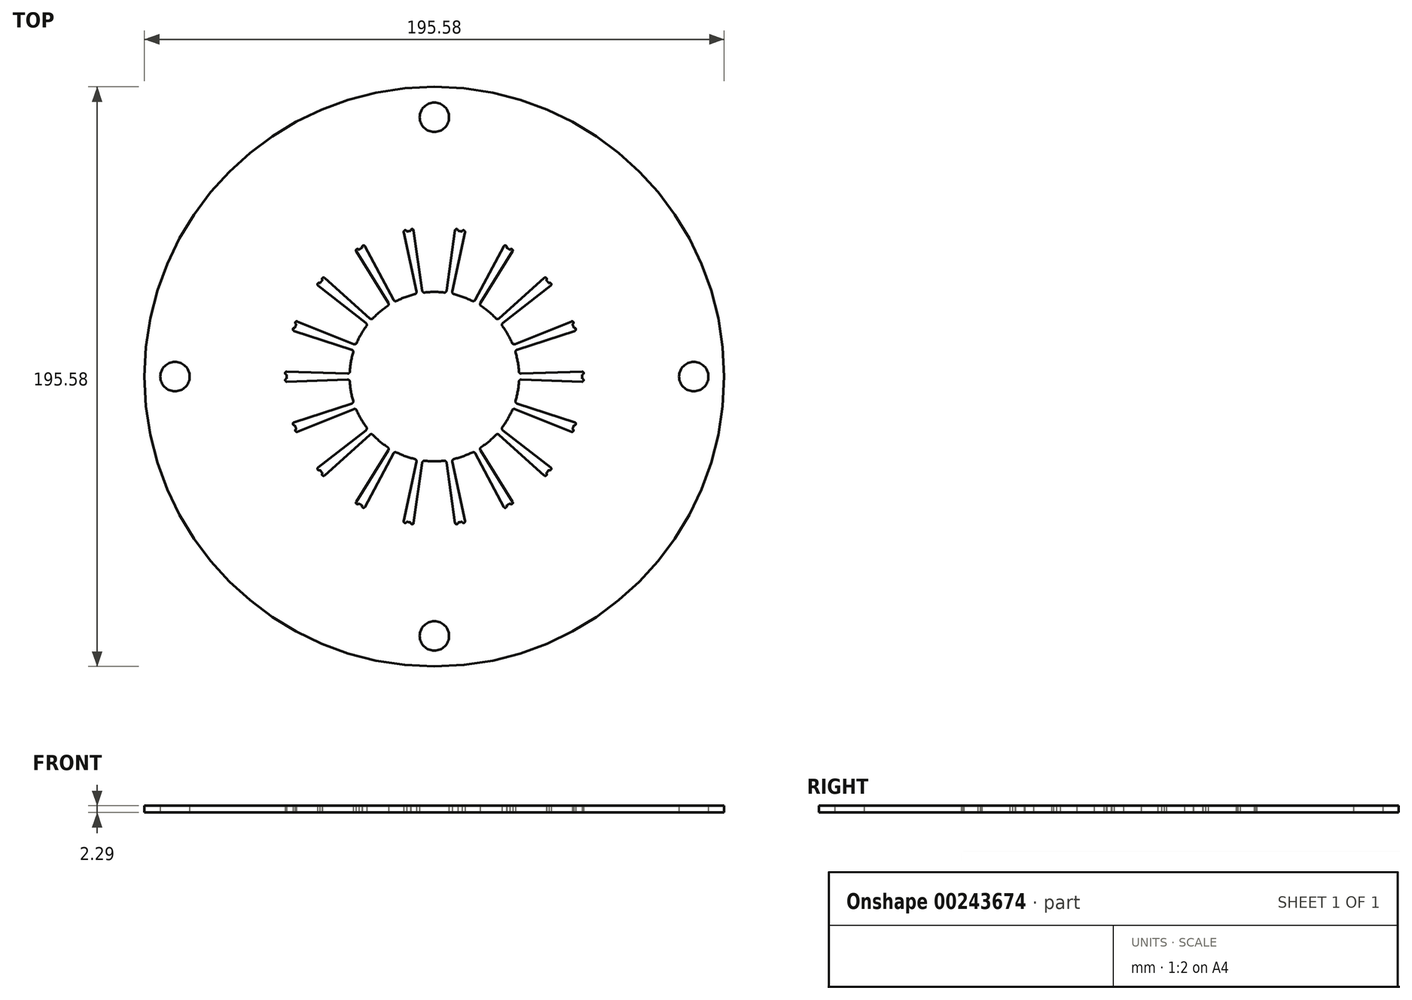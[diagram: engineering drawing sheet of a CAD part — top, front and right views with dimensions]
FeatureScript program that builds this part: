
annotation { "Feature Type Name" : "Feature", "Feature Type Description" : "" }
export const myFeature = defineFeature(function(context is Context, id is Id, definition is map)
    precondition{}
    {
        {
            var Q0;
            Q0=qCreatedBy(makeId("Top.planeOp"),FACE);
            var sketch = newSketch(context, id + "F0", { "sketchPlane" : qUnion([Q0])});
            skCircle(sketch, "E0", {"center": v(0, 0) * mm, "radius": 97.8 * mm});
            skLineSegment(sketch, "E1", {"start": v(0, 0) * mm, "end": v(0, 87.5) * mm, "construction": true});
            skCircle(sketch, "E2", {"center": v(0, 87.5) * mm, "radius": 4.95 * mm});
            skCircle(sketch, "E3.1.0", {"center": v(-87.5, 0) * mm, "radius": 4.95 * mm});
            skCircle(sketch, "E3.2.0", {"center": v(0, -87.5) * mm, "radius": 4.95 * mm});
            skCircle(sketch, "E3.3.0", {"center": v(87.5, 0) * mm, "radius": 4.95 * mm});
            skCircle(sketch, "E4", {"center": v(0, 0) * mm, "radius": 49.85 * mm});
            skCircle(sketch, "E5", {"center": v(0, 0) * mm, "radius": 12.7 * mm});
            skLineSegment(sketch, "E6", {"start": v(-6.99, 49.36) * mm, "end": v(-1.78, 12.57) * mm});
            skLineSegment(sketch, "E7", {"start": v(1.78, 12.57) * mm, "end": v(6.98, 49.36) * mm});
            skLineSegment(sketch, "E8", {"start": v(6.98, 49.36) * mm, "end": v(0, 50.34) * mm, "construction": true});
            skLineSegment(sketch, "E9", {"start": v(0, 50.34) * mm, "end": v(-6.99, 49.36) * mm, "construction": true});
            skLineSegment(sketch, "E10", {"start": v(-6.99, 49.36) * mm, "end": v(6.99, 49.36) * mm, "construction": true});
            skCircle(sketch, "E11", {"center": v(0, 0) * mm, "radius": 28.58 * mm});
            skLineSegment(sketch, "E12.1.0", {"start": v(-23.44, 44) * mm, "end": v(-5.97, 11.2) * mm});
            skLineSegment(sketch, "E12.1.1", {"start": v(-2.63, 12.43) * mm, "end": v(-10.32, 48.77) * mm});
            skLineSegment(sketch, "E12.2.0", {"start": v(-37.08, 33.32) * mm, "end": v(-9.45, 8.49) * mm});
            skLineSegment(sketch, "E12.2.1", {"start": v(-6.72, 10.78) * mm, "end": v(-26.37, 42.3) * mm});
            skLineSegment(sketch, "E12.3.0", {"start": v(-46.24, 18.63) * mm, "end": v(-11.78, 4.75) * mm});
            skLineSegment(sketch, "E12.3.1", {"start": v(-10, 7.83) * mm, "end": v(-39.25, 30.73) * mm});
            skLineSegment(sketch, "E12.4.0", {"start": v(-49.82, 1.7) * mm, "end": v(-12.7, 0.43) * mm});
            skLineSegment(sketch, "E12.4.1", {"start": v(-12.07, 3.94) * mm, "end": v(-47.4, 15.45) * mm});
            skLineSegment(sketch, "E12.5.0", {"start": v(-47.4, -15.45) * mm, "end": v(-12.07, -3.94) * mm});
            skLineSegment(sketch, "E12.5.1", {"start": v(-12.7, -0.43) * mm, "end": v(-49.82, -1.7) * mm});
            skLineSegment(sketch, "E12.6.0", {"start": v(-39.25, -30.73) * mm, "end": v(-10, -7.83) * mm});
            skLineSegment(sketch, "E12.6.1", {"start": v(-11.78, -4.75) * mm, "end": v(-46.24, -18.63) * mm});
            skLineSegment(sketch, "E12.7.0", {"start": v(-26.37, -42.3) * mm, "end": v(-6.72, -10.78) * mm});
            skLineSegment(sketch, "E12.7.1", {"start": v(-9.45, -8.49) * mm, "end": v(-37.08, -33.32) * mm});
            skLineSegment(sketch, "E12.8.0", {"start": v(-10.32, -48.77) * mm, "end": v(-2.63, -12.43) * mm});
            skLineSegment(sketch, "E12.8.1", {"start": v(-5.97, -11.2) * mm, "end": v(-23.44, -44) * mm});
            skLineSegment(sketch, "E12.9.0", {"start": v(6.98, -49.36) * mm, "end": v(1.78, -12.57) * mm});
            skLineSegment(sketch, "E12.9.1", {"start": v(-1.78, -12.57) * mm, "end": v(-6.99, -49.36) * mm});
            skLineSegment(sketch, "E12.10.0", {"start": v(23.44, -44) * mm, "end": v(5.97, -11.2) * mm});
            skLineSegment(sketch, "E12.10.1", {"start": v(2.63, -12.43) * mm, "end": v(10.32, -48.77) * mm});
            skLineSegment(sketch, "E12.11.0", {"start": v(37.08, -33.32) * mm, "end": v(9.45, -8.49) * mm});
            skLineSegment(sketch, "E12.11.1", {"start": v(6.72, -10.78) * mm, "end": v(26.37, -42.3) * mm});
            skLineSegment(sketch, "E12.12.0", {"start": v(46.24, -18.63) * mm, "end": v(11.78, -4.75) * mm});
            skLineSegment(sketch, "E12.12.1", {"start": v(10, -7.83) * mm, "end": v(39.25, -30.73) * mm});
            skLineSegment(sketch, "E12.13.0", {"start": v(49.82, -1.7) * mm, "end": v(12.7, -0.43) * mm});
            skLineSegment(sketch, "E12.13.1", {"start": v(12.07, -3.94) * mm, "end": v(47.4, -15.45) * mm});
            skLineSegment(sketch, "E12.14.0", {"start": v(47.4, 15.45) * mm, "end": v(12.07, 3.94) * mm});
            skLineSegment(sketch, "E12.14.1", {"start": v(12.7, 0.43) * mm, "end": v(49.82, 1.7) * mm});
            skLineSegment(sketch, "E12.15.0", {"start": v(39.25, 30.73) * mm, "end": v(10, 7.83) * mm});
            skLineSegment(sketch, "E12.15.1", {"start": v(11.78, 4.75) * mm, "end": v(46.24, 18.63) * mm});
            skLineSegment(sketch, "E12.16.0", {"start": v(26.37, 42.3) * mm, "end": v(6.72, 10.78) * mm});
            skLineSegment(sketch, "E12.16.1", {"start": v(9.45, 8.49) * mm, "end": v(37.08, 33.32) * mm});
            skLineSegment(sketch, "E12.17.0", {"start": v(10.32, 48.77) * mm, "end": v(2.63, 12.43) * mm});
            skLineSegment(sketch, "E12.17.1", {"start": v(5.97, 11.2) * mm, "end": v(23.44, 44) * mm});
            skSolve(sketch);
        }
        {
            var Q0;
            Q0=makeQuery(id+"F0.imprint","IMPRINT",FACE,{"disambiguationData":[TD([[makeQuery(id+"F0.imprint","IMPRINT",EDGE,{"derivedFrom":sQuery(id+"F0.wireOp",EDGE,"E0")}),1.0]])]});
            var Q1;
            {var subQ0=sQuery(id+"F0.wireOp",EDGE,"E12.15.0");var subQ1=sQuery(id+"F0.wireOp",EDGE,"E4");var subQ2=makeQuery(id+"F0.imprint","INTERSECT",VERTEX,{"derivedFrom":[subQ1,subQ0]});Q1=makeQuery(id+"F0.imprint","IMPRINT",FACE,{"disambiguationData":[TD([[makeQuery(id+"F0.imprint","IMPRINT",EDGE,{"disambiguationData":[TD([[subQ2,1.0]])],"derivedFrom":subQ1}),1.0]])]});}
            var Q2;
            {var subQ0=sQuery(id+"F0.wireOp",EDGE,"E12.16.0");var subQ1=sQuery(id+"F0.wireOp",EDGE,"E4");var subQ2=makeQuery(id+"F0.imprint","INTERSECT",VERTEX,{"derivedFrom":[subQ1,subQ0]});Q2=makeQuery(id+"F0.imprint","IMPRINT",FACE,{"disambiguationData":[TD([[makeQuery(id+"F0.imprint","IMPRINT",EDGE,{"disambiguationData":[TD([[subQ2,1.0]])],"derivedFrom":subQ1}),1.0]])]});}
            var Q3;
            {var subQ0=sQuery(id+"F0.wireOp",EDGE,"E12.17.0");var subQ1=sQuery(id+"F0.wireOp",EDGE,"E4");var subQ2=makeQuery(id+"F0.imprint","INTERSECT",VERTEX,{"derivedFrom":[subQ1,subQ0]});Q3=makeQuery(id+"F0.imprint","IMPRINT",FACE,{"disambiguationData":[TD([[makeQuery(id+"F0.imprint","IMPRINT",EDGE,{"disambiguationData":[TD([[subQ2,1.0]])],"derivedFrom":subQ1}),1.0]])]});}
            var Q4;
            {var subQ0=sQuery(id+"F0.wireOp",EDGE,"E6");var subQ1=sQuery(id+"F0.wireOp",EDGE,"E4");var subQ2=makeQuery(id+"F0.imprint","INTERSECT",VERTEX,{"derivedFrom":[subQ1,subQ0]});Q4=makeQuery(id+"F0.imprint","IMPRINT",FACE,{"disambiguationData":[TD([[makeQuery(id+"F0.imprint","IMPRINT",EDGE,{"disambiguationData":[TD([[subQ2,1.0]])],"derivedFrom":subQ1}),1.0]])]});}
            var Q5;
            {var subQ0=sQuery(id+"F0.wireOp",EDGE,"E12.1.0");var subQ1=sQuery(id+"F0.wireOp",EDGE,"E4");var subQ2=makeQuery(id+"F0.imprint","INTERSECT",VERTEX,{"derivedFrom":[subQ1,subQ0]});Q5=makeQuery(id+"F0.imprint","IMPRINT",FACE,{"disambiguationData":[TD([[makeQuery(id+"F0.imprint","IMPRINT",EDGE,{"disambiguationData":[TD([[subQ2,1.0]])],"derivedFrom":subQ1}),1.0]])]});}
            var Q6;
            {var subQ0=sQuery(id+"F0.wireOp",EDGE,"E12.2.0");var subQ1=sQuery(id+"F0.wireOp",EDGE,"E4");var subQ2=makeQuery(id+"F0.imprint","INTERSECT",VERTEX,{"derivedFrom":[subQ1,subQ0]});Q6=makeQuery(id+"F0.imprint","IMPRINT",FACE,{"disambiguationData":[TD([[makeQuery(id+"F0.imprint","IMPRINT",EDGE,{"disambiguationData":[TD([[subQ2,1.0]])],"derivedFrom":subQ1}),1.0]])]});}
            var Q7;
            {var subQ0=sQuery(id+"F0.wireOp",EDGE,"E12.3.0");var subQ1=sQuery(id+"F0.wireOp",EDGE,"E4");var subQ2=makeQuery(id+"F0.imprint","INTERSECT",VERTEX,{"derivedFrom":[subQ1,subQ0]});Q7=makeQuery(id+"F0.imprint","IMPRINT",FACE,{"disambiguationData":[TD([[makeQuery(id+"F0.imprint","IMPRINT",EDGE,{"disambiguationData":[TD([[subQ2,1.0]])],"derivedFrom":subQ1}),1.0]])]});}
            var Q8;
            {var subQ0=sQuery(id+"F0.wireOp",EDGE,"E12.4.0");var subQ1=sQuery(id+"F0.wireOp",EDGE,"E4");var subQ2=makeQuery(id+"F0.imprint","INTERSECT",VERTEX,{"derivedFrom":[subQ1,subQ0]});Q8=makeQuery(id+"F0.imprint","IMPRINT",FACE,{"disambiguationData":[TD([[makeQuery(id+"F0.imprint","IMPRINT",EDGE,{"disambiguationData":[TD([[subQ2,1.0]])],"derivedFrom":subQ1}),1.0]])]});}
            var Q9;
            {var subQ0=sQuery(id+"F0.wireOp",EDGE,"E12.5.0");var subQ1=sQuery(id+"F0.wireOp",EDGE,"E4");var subQ2=makeQuery(id+"F0.imprint","INTERSECT",VERTEX,{"derivedFrom":[subQ1,subQ0]});Q9=makeQuery(id+"F0.imprint","IMPRINT",FACE,{"disambiguationData":[TD([[makeQuery(id+"F0.imprint","IMPRINT",EDGE,{"disambiguationData":[TD([[subQ2,1.0]])],"derivedFrom":subQ1}),1.0]])]});}
            var Q10;
            {var subQ0=sQuery(id+"F0.wireOp",EDGE,"E12.6.0");var subQ1=sQuery(id+"F0.wireOp",EDGE,"E4");var subQ2=makeQuery(id+"F0.imprint","INTERSECT",VERTEX,{"derivedFrom":[subQ1,subQ0]});Q10=makeQuery(id+"F0.imprint","IMPRINT",FACE,{"disambiguationData":[TD([[makeQuery(id+"F0.imprint","IMPRINT",EDGE,{"disambiguationData":[TD([[subQ2,1.0]])],"derivedFrom":subQ1}),1.0]])]});}
            var Q11;
            {var subQ0=sQuery(id+"F0.wireOp",EDGE,"E12.7.0");var subQ1=sQuery(id+"F0.wireOp",EDGE,"E4");var subQ2=makeQuery(id+"F0.imprint","INTERSECT",VERTEX,{"derivedFrom":[subQ1,subQ0]});Q11=makeQuery(id+"F0.imprint","IMPRINT",FACE,{"disambiguationData":[TD([[makeQuery(id+"F0.imprint","IMPRINT",EDGE,{"disambiguationData":[TD([[subQ2,1.0]])],"derivedFrom":subQ1}),1.0]])]});}
            var Q12;
            {var subQ0=sQuery(id+"F0.wireOp",EDGE,"E12.8.0");var subQ1=sQuery(id+"F0.wireOp",EDGE,"E4");var subQ2=makeQuery(id+"F0.imprint","INTERSECT",VERTEX,{"derivedFrom":[subQ1,subQ0]});Q12=makeQuery(id+"F0.imprint","IMPRINT",FACE,{"disambiguationData":[TD([[makeQuery(id+"F0.imprint","IMPRINT",EDGE,{"disambiguationData":[TD([[subQ2,1.0]])],"derivedFrom":subQ1}),1.0]])]});}
            var Q13;
            {var subQ0=sQuery(id+"F0.wireOp",EDGE,"E12.9.0");var subQ1=sQuery(id+"F0.wireOp",EDGE,"E4");var subQ2=makeQuery(id+"F0.imprint","INTERSECT",VERTEX,{"derivedFrom":[subQ1,subQ0]});Q13=makeQuery(id+"F0.imprint","IMPRINT",FACE,{"disambiguationData":[TD([[makeQuery(id+"F0.imprint","IMPRINT",EDGE,{"disambiguationData":[TD([[subQ2,1.0]])],"derivedFrom":subQ1}),1.0]])]});}
            var Q14;
            {var subQ0=sQuery(id+"F0.wireOp",EDGE,"E12.10.0");var subQ1=sQuery(id+"F0.wireOp",EDGE,"E4");var subQ2=makeQuery(id+"F0.imprint","INTERSECT",VERTEX,{"derivedFrom":[subQ1,subQ0]});Q14=makeQuery(id+"F0.imprint","IMPRINT",FACE,{"disambiguationData":[TD([[makeQuery(id+"F0.imprint","IMPRINT",EDGE,{"disambiguationData":[TD([[subQ2,1.0]])],"derivedFrom":subQ1}),1.0]])]});}
            var Q15;
            {var subQ0=sQuery(id+"F0.wireOp",EDGE,"E12.11.0");var subQ1=sQuery(id+"F0.wireOp",EDGE,"E4");var subQ2=makeQuery(id+"F0.imprint","INTERSECT",VERTEX,{"derivedFrom":[subQ1,subQ0]});Q15=makeQuery(id+"F0.imprint","IMPRINT",FACE,{"disambiguationData":[TD([[makeQuery(id+"F0.imprint","IMPRINT",EDGE,{"disambiguationData":[TD([[subQ2,1.0]])],"derivedFrom":subQ1}),1.0]])]});}
            var Q16;
            {var subQ0=sQuery(id+"F0.wireOp",EDGE,"E12.12.0");var subQ1=sQuery(id+"F0.wireOp",EDGE,"E4");var subQ2=makeQuery(id+"F0.imprint","INTERSECT",VERTEX,{"derivedFrom":[subQ1,subQ0]});Q16=makeQuery(id+"F0.imprint","IMPRINT",FACE,{"disambiguationData":[TD([[makeQuery(id+"F0.imprint","IMPRINT",EDGE,{"disambiguationData":[TD([[subQ2,1.0]])],"derivedFrom":subQ1}),1.0]])]});}
            var Q17;
            {var subQ0=sQuery(id+"F0.wireOp",EDGE,"E12.13.0");var subQ1=sQuery(id+"F0.wireOp",EDGE,"E4");var subQ2=makeQuery(id+"F0.imprint","INTERSECT",VERTEX,{"derivedFrom":[subQ1,subQ0]});Q17=makeQuery(id+"F0.imprint","IMPRINT",FACE,{"disambiguationData":[TD([[makeQuery(id+"F0.imprint","IMPRINT",EDGE,{"disambiguationData":[TD([[subQ2,1.0]])],"derivedFrom":subQ1}),1.0]])]});}
            var Q18;
            {var subQ0=sQuery(id+"F0.wireOp",EDGE,"E12.14.0");var subQ1=sQuery(id+"F0.wireOp",EDGE,"E4");var subQ2=makeQuery(id+"F0.imprint","INTERSECT",VERTEX,{"derivedFrom":[subQ1,subQ0]});Q18=makeQuery(id+"F0.imprint","IMPRINT",FACE,{"disambiguationData":[TD([[makeQuery(id+"F0.imprint","IMPRINT",EDGE,{"disambiguationData":[TD([[subQ2,1.0]])],"derivedFrom":subQ1}),1.0]])]});}
            extrude(context, id + "F1", {"entities" : qUnion([Q0, Q1, Q2, Q3, Q4, Q5, Q6, Q7, Q8, Q9, Q10, Q11, Q12, Q13, Q14, Q15, Q16, Q17, Q18]), "depth" : 2.3 * mm});
        }
        {
            var Q0;
            Q0=makeQuery(id+"F1.opExtrude","CAP_FACE",FACE,{"disambiguationData":[OSD([sQuery(id+"F0.wireOp",EDGE,"E0"),sQuery(id+"F0.wireOp",EDGE,"E2"),sQuery(id+"F0.wireOp",EDGE,"E3.1.0"),sQuery(id+"F0.wireOp",EDGE,"E3.2.0"),sQuery(id+"F0.wireOp",EDGE,"E3.3.0"),sQuery(id+"F0.wireOp",EDGE,"E4"),sQuery(id+"F0.wireOp",EDGE,"E6"),sQuery(id+"F0.wireOp",EDGE,"E7"),sQuery(id+"F0.wireOp",EDGE,"E11"),sQuery(id+"F0.wireOp",EDGE,"E12.1.0"),sQuery(id+"F0.wireOp",EDGE,"E12.1.1"),sQuery(id+"F0.wireOp",EDGE,"E12.2.0"),sQuery(id+"F0.wireOp",EDGE,"E12.2.1"),sQuery(id+"F0.wireOp",EDGE,"E12.3.0"),sQuery(id+"F0.wireOp",EDGE,"E12.3.1"),sQuery(id+"F0.wireOp",EDGE,"E12.4.0"),sQuery(id+"F0.wireOp",EDGE,"E12.4.1"),sQuery(id+"F0.wireOp",EDGE,"E12.5.0"),sQuery(id+"F0.wireOp",EDGE,"E12.5.1"),sQuery(id+"F0.wireOp",EDGE,"E12.6.0"),sQuery(id+"F0.wireOp",EDGE,"E12.6.1"),sQuery(id+"F0.wireOp",EDGE,"E12.7.0"),sQuery(id+"F0.wireOp",EDGE,"E12.7.1"),sQuery(id+"F0.wireOp",EDGE,"E12.8.0"),sQuery(id+"F0.wireOp",EDGE,"E12.8.1"),sQuery(id+"F0.wireOp",EDGE,"E12.9.0"),sQuery(id+"F0.wireOp",EDGE,"E12.9.1"),sQuery(id+"F0.wireOp",EDGE,"E12.10.0"),sQuery(id+"F0.wireOp",EDGE,"E12.10.1"),sQuery(id+"F0.wireOp",EDGE,"E12.11.0"),sQuery(id+"F0.wireOp",EDGE,"E12.11.1"),sQuery(id+"F0.wireOp",EDGE,"E12.12.0"),sQuery(id+"F0.wireOp",EDGE,"E12.12.1"),sQuery(id+"F0.wireOp",EDGE,"E12.13.0"),sQuery(id+"F0.wireOp",EDGE,"E12.13.1"),sQuery(id+"F0.wireOp",EDGE,"E12.14.0"),sQuery(id+"F0.wireOp",EDGE,"E12.14.1"),sQuery(id+"F0.wireOp",EDGE,"E12.15.0"),sQuery(id+"F0.wireOp",EDGE,"E12.15.1"),sQuery(id+"F0.wireOp",EDGE,"E12.16.0"),sQuery(id+"F0.wireOp",EDGE,"E12.16.1"),sQuery(id+"F0.wireOp",EDGE,"E12.17.0"),sQuery(id+"F0.wireOp",EDGE,"E12.17.1")])],"isStart":true});
            var sketch = newSketch(context, id + "F2", { "sketchPlane" : qUnion([Q0])});
            skArc(sketch, "E13", {"start": v(-7.99, -49.2) * mm, "mid": v(-7.56, -49.79) * mm, "end": v(-6.98, -49.36) * mm});
            skArc(sketch, "E14", {"start": v(-10.32, -48.77) * mm, "mid": v(-9.92, -49.37) * mm, "end": v(-9.32, -48.97) * mm});
            skCircle(sketch, "E15", {"center": v(0, 0) * mm, "radius": 49.85 * mm});
            skArc(sketch, "E16.1.0", {"start": v(6.99, -49.36) * mm, "mid": v(7.56, -49.79) * mm, "end": v(7.99, -49.2) * mm});
            skArc(sketch, "E16.1.1", {"start": v(9.32, -48.97) * mm, "mid": v(9.92, -49.37) * mm, "end": v(10.32, -48.77) * mm});
            skArc(sketch, "E16.2.0", {"start": v(23.44, -44) * mm, "mid": v(24.14, -44.2) * mm, "end": v(24.34, -43.5) * mm});
            skArc(sketch, "E16.2.1", {"start": v(25.5, -42.83) * mm, "mid": v(26.2, -43) * mm, "end": v(26.37, -42.3) * mm});
            skArc(sketch, "E16.3.0", {"start": v(37.08, -33.32) * mm, "mid": v(37.8, -33.28) * mm, "end": v(37.75, -32.56) * mm});
            skArc(sketch, "E16.3.1", {"start": v(38.62, -31.52) * mm, "mid": v(39.33, -31.44) * mm, "end": v(39.25, -30.73) * mm});
            skArc(sketch, "E16.4.0", {"start": v(46.24, -18.63) * mm, "mid": v(46.9, -18.34) * mm, "end": v(46.6, -17.68) * mm});
            skArc(sketch, "E16.4.1", {"start": v(47.07, -16.41) * mm, "mid": v(47.72, -16.1) * mm, "end": v(47.4, -15.45) * mm});
            skArc(sketch, "E16.5.0", {"start": v(49.82, -1.7) * mm, "mid": v(50.34, -1.2) * mm, "end": v(49.84, -0.68) * mm});
            skArc(sketch, "E16.5.1", {"start": v(49.84, 0.68) * mm, "mid": v(50.34, 1.2) * mm, "end": v(49.82, 1.7) * mm});
            skArc(sketch, "E16.6.0", {"start": v(47.4, 15.45) * mm, "mid": v(47.72, 16.1) * mm, "end": v(47.07, 16.41) * mm});
            skArc(sketch, "E16.6.1", {"start": v(46.6, 17.68) * mm, "mid": v(46.9, 18.34) * mm, "end": v(46.24, 18.63) * mm});
            skArc(sketch, "E16.7.0", {"start": v(39.25, 30.73) * mm, "mid": v(39.33, 31.44) * mm, "end": v(38.62, 31.52) * mm});
            skArc(sketch, "E16.7.1", {"start": v(37.75, 32.56) * mm, "mid": v(37.8, 33.28) * mm, "end": v(37.08, 33.32) * mm});
            skArc(sketch, "E16.8.0", {"start": v(26.37, 42.3) * mm, "mid": v(26.2, 43) * mm, "end": v(25.5, 42.83) * mm});
            skArc(sketch, "E16.8.1", {"start": v(24.34, 43.5) * mm, "mid": v(24.14, 44.2) * mm, "end": v(23.44, 44) * mm});
            skArc(sketch, "E16.9.0", {"start": v(10.32, 48.77) * mm, "mid": v(9.92, 49.37) * mm, "end": v(9.32, 48.97) * mm});
            skArc(sketch, "E16.9.1", {"start": v(7.99, 49.2) * mm, "mid": v(7.56, 49.79) * mm, "end": v(6.99, 49.36) * mm});
            skArc(sketch, "E16.10.0", {"start": v(-6.99, 49.36) * mm, "mid": v(-7.56, 49.79) * mm, "end": v(-7.99, 49.2) * mm});
            skArc(sketch, "E16.10.1", {"start": v(-9.32, 48.97) * mm, "mid": v(-9.92, 49.37) * mm, "end": v(-10.32, 48.77) * mm});
            skArc(sketch, "E16.11.0", {"start": v(-23.44, 44) * mm, "mid": v(-24.14, 44.2) * mm, "end": v(-24.34, 43.5) * mm});
            skArc(sketch, "E16.11.1", {"start": v(-25.5, 42.83) * mm, "mid": v(-26.2, 43) * mm, "end": v(-26.37, 42.3) * mm});
            skArc(sketch, "E16.12.0", {"start": v(-37.08, 33.32) * mm, "mid": v(-37.8, 33.28) * mm, "end": v(-37.75, 32.56) * mm});
            skArc(sketch, "E16.12.1", {"start": v(-38.62, 31.52) * mm, "mid": v(-39.33, 31.44) * mm, "end": v(-39.25, 30.73) * mm});
            skArc(sketch, "E16.13.0", {"start": v(-46.24, 18.63) * mm, "mid": v(-46.9, 18.34) * mm, "end": v(-46.6, 17.68) * mm});
            skArc(sketch, "E16.13.1", {"start": v(-47.07, 16.41) * mm, "mid": v(-47.72, 16.1) * mm, "end": v(-47.4, 15.45) * mm});
            skArc(sketch, "E16.14.0", {"start": v(-49.82, 1.7) * mm, "mid": v(-50.34, 1.2) * mm, "end": v(-49.84, 0.68) * mm});
            skArc(sketch, "E16.14.1", {"start": v(-49.84, -0.68) * mm, "mid": v(-50.34, -1.2) * mm, "end": v(-49.82, -1.7) * mm});
            skArc(sketch, "E16.15.0", {"start": v(-47.4, -15.45) * mm, "mid": v(-47.72, -16.1) * mm, "end": v(-47.07, -16.41) * mm});
            skArc(sketch, "E16.15.1", {"start": v(-46.6, -17.68) * mm, "mid": v(-46.9, -18.34) * mm, "end": v(-46.24, -18.63) * mm});
            skArc(sketch, "E16.16.0", {"start": v(-39.25, -30.73) * mm, "mid": v(-39.33, -31.44) * mm, "end": v(-38.62, -31.52) * mm});
            skArc(sketch, "E16.16.1", {"start": v(-37.75, -32.56) * mm, "mid": v(-37.8, -33.28) * mm, "end": v(-37.08, -33.32) * mm});
            skArc(sketch, "E16.17.0", {"start": v(-26.37, -42.3) * mm, "mid": v(-26.2, -43) * mm, "end": v(-25.5, -42.83) * mm});
            skArc(sketch, "E16.17.1", {"start": v(-24.34, -43.5) * mm, "mid": v(-24.14, -44.2) * mm, "end": v(-23.44, -44) * mm});
            skSolve(sketch);
        }
        {
            var Q0;
            {var subQ0=sQuery(id+"F2.wireOp",EDGE,"E16.4.0");Q0=makeQuery(id+"F2.imprint","IMPRINT",FACE,{"disambiguationData":[TD([[makeQuery(id+"F2.imprint","IMPRINT",EDGE,{"derivedFrom":subQ0}),1.0]])]});}
            var Q1;
            {var subQ0=sQuery(id+"F2.wireOp",EDGE,"E16.3.1");Q1=makeQuery(id+"F2.imprint","IMPRINT",FACE,{"disambiguationData":[TD([[makeQuery(id+"F2.imprint","IMPRINT",EDGE,{"derivedFrom":subQ0}),1.0]])]});}
            var Q2;
            {var subQ0=sQuery(id+"F2.wireOp",EDGE,"E16.3.0");Q2=makeQuery(id+"F2.imprint","IMPRINT",FACE,{"disambiguationData":[TD([[makeQuery(id+"F2.imprint","IMPRINT",EDGE,{"derivedFrom":subQ0}),1.0]])]});}
            var Q3;
            {var subQ0=sQuery(id+"F2.wireOp",EDGE,"E16.2.1");Q3=makeQuery(id+"F2.imprint","IMPRINT",FACE,{"disambiguationData":[TD([[makeQuery(id+"F2.imprint","IMPRINT",EDGE,{"derivedFrom":subQ0}),1.0]])]});}
            var Q4;
            {var subQ0=sQuery(id+"F2.wireOp",EDGE,"E16.2.0");Q4=makeQuery(id+"F2.imprint","IMPRINT",FACE,{"disambiguationData":[TD([[makeQuery(id+"F2.imprint","IMPRINT",EDGE,{"derivedFrom":subQ0}),1.0]])]});}
            var Q5;
            {var subQ0=sQuery(id+"F2.wireOp",EDGE,"E16.1.0");Q5=makeQuery(id+"F2.imprint","IMPRINT",FACE,{"disambiguationData":[TD([[makeQuery(id+"F2.imprint","IMPRINT",EDGE,{"derivedFrom":subQ0}),1.0]])]});}
            var Q6;
            {var subQ0=sQuery(id+"F2.wireOp",EDGE,"E16.1.1");Q6=makeQuery(id+"F2.imprint","IMPRINT",FACE,{"disambiguationData":[TD([[makeQuery(id+"F2.imprint","IMPRINT",EDGE,{"derivedFrom":subQ0}),1.0]])]});}
            var Q7;
            {var subQ0=sQuery(id+"F2.wireOp",EDGE,"E13");Q7=makeQuery(id+"F2.imprint","IMPRINT",FACE,{"disambiguationData":[TD([[makeQuery(id+"F2.imprint","IMPRINT",EDGE,{"derivedFrom":subQ0}),1.0]])]});}
            var Q8;
            {var subQ0=sQuery(id+"F2.wireOp",EDGE,"E14");Q8=makeQuery(id+"F2.imprint","IMPRINT",FACE,{"disambiguationData":[TD([[makeQuery(id+"F2.imprint","IMPRINT",EDGE,{"derivedFrom":subQ0}),1.0]])]});}
            var Q9;
            {var subQ0=sQuery(id+"F2.wireOp",EDGE,"E16.17.1");Q9=makeQuery(id+"F2.imprint","IMPRINT",FACE,{"disambiguationData":[TD([[makeQuery(id+"F2.imprint","IMPRINT",EDGE,{"derivedFrom":subQ0}),1.0]])]});}
            var Q10;
            {var subQ0=sQuery(id+"F2.wireOp",EDGE,"E16.17.0");Q10=makeQuery(id+"F2.imprint","IMPRINT",FACE,{"disambiguationData":[TD([[makeQuery(id+"F2.imprint","IMPRINT",EDGE,{"derivedFrom":subQ0}),1.0]])]});}
            var Q11;
            {var subQ0=sQuery(id+"F2.wireOp",EDGE,"E16.16.1");Q11=makeQuery(id+"F2.imprint","IMPRINT",FACE,{"disambiguationData":[TD([[makeQuery(id+"F2.imprint","IMPRINT",EDGE,{"derivedFrom":subQ0}),1.0]])]});}
            var Q12;
            {var subQ0=sQuery(id+"F2.wireOp",EDGE,"E16.16.0");Q12=makeQuery(id+"F2.imprint","IMPRINT",FACE,{"disambiguationData":[TD([[makeQuery(id+"F2.imprint","IMPRINT",EDGE,{"derivedFrom":subQ0}),1.0]])]});}
            var Q13;
            {var subQ0=sQuery(id+"F2.wireOp",EDGE,"E16.15.1");Q13=makeQuery(id+"F2.imprint","IMPRINT",FACE,{"disambiguationData":[TD([[makeQuery(id+"F2.imprint","IMPRINT",EDGE,{"derivedFrom":subQ0}),1.0]])]});}
            var Q14;
            {var subQ0=sQuery(id+"F2.wireOp",EDGE,"E16.15.0");Q14=makeQuery(id+"F2.imprint","IMPRINT",FACE,{"disambiguationData":[TD([[makeQuery(id+"F2.imprint","IMPRINT",EDGE,{"derivedFrom":subQ0}),1.0]])]});}
            var Q15;
            {var subQ0=sQuery(id+"F2.wireOp",EDGE,"E16.14.1");Q15=makeQuery(id+"F2.imprint","IMPRINT",FACE,{"disambiguationData":[TD([[makeQuery(id+"F2.imprint","IMPRINT",EDGE,{"derivedFrom":subQ0}),1.0]])]});}
            var Q16;
            {var subQ0=sQuery(id+"F2.wireOp",EDGE,"E16.14.0");Q16=makeQuery(id+"F2.imprint","IMPRINT",FACE,{"disambiguationData":[TD([[makeQuery(id+"F2.imprint","IMPRINT",EDGE,{"derivedFrom":subQ0}),1.0]])]});}
            var Q17;
            {var subQ0=sQuery(id+"F2.wireOp",EDGE,"E16.13.0");Q17=makeQuery(id+"F2.imprint","IMPRINT",FACE,{"disambiguationData":[TD([[makeQuery(id+"F2.imprint","IMPRINT",EDGE,{"derivedFrom":subQ0}),1.0]])]});}
            var Q18;
            {var subQ0=sQuery(id+"F2.wireOp",EDGE,"E16.13.1");Q18=makeQuery(id+"F2.imprint","IMPRINT",FACE,{"disambiguationData":[TD([[makeQuery(id+"F2.imprint","IMPRINT",EDGE,{"derivedFrom":subQ0}),1.0]])]});}
            var Q19;
            {var subQ0=sQuery(id+"F2.wireOp",EDGE,"E16.12.0");Q19=makeQuery(id+"F2.imprint","IMPRINT",FACE,{"disambiguationData":[TD([[makeQuery(id+"F2.imprint","IMPRINT",EDGE,{"derivedFrom":subQ0}),1.0]])]});}
            var Q20;
            {var subQ0=sQuery(id+"F2.wireOp",EDGE,"E16.12.1");Q20=makeQuery(id+"F2.imprint","IMPRINT",FACE,{"disambiguationData":[TD([[makeQuery(id+"F2.imprint","IMPRINT",EDGE,{"derivedFrom":subQ0}),1.0]])]});}
            var Q21;
            {var subQ0=sQuery(id+"F2.wireOp",EDGE,"E16.11.1");Q21=makeQuery(id+"F2.imprint","IMPRINT",FACE,{"disambiguationData":[TD([[makeQuery(id+"F2.imprint","IMPRINT",EDGE,{"derivedFrom":subQ0}),1.0]])]});}
            var Q22;
            {var subQ0=sQuery(id+"F2.wireOp",EDGE,"E16.11.0");Q22=makeQuery(id+"F2.imprint","IMPRINT",FACE,{"disambiguationData":[TD([[makeQuery(id+"F2.imprint","IMPRINT",EDGE,{"derivedFrom":subQ0}),1.0]])]});}
            var Q23;
            {var subQ0=sQuery(id+"F2.wireOp",EDGE,"E16.10.1");Q23=makeQuery(id+"F2.imprint","IMPRINT",FACE,{"disambiguationData":[TD([[makeQuery(id+"F2.imprint","IMPRINT",EDGE,{"derivedFrom":subQ0}),1.0]])]});}
            var Q24;
            {var subQ0=sQuery(id+"F2.wireOp",EDGE,"E16.10.0");Q24=makeQuery(id+"F2.imprint","IMPRINT",FACE,{"disambiguationData":[TD([[makeQuery(id+"F2.imprint","IMPRINT",EDGE,{"derivedFrom":subQ0}),1.0]])]});}
            var Q25;
            {var subQ0=sQuery(id+"F2.wireOp",EDGE,"E16.9.1");Q25=makeQuery(id+"F2.imprint","IMPRINT",FACE,{"disambiguationData":[TD([[makeQuery(id+"F2.imprint","IMPRINT",EDGE,{"derivedFrom":subQ0}),1.0]])]});}
            var Q26;
            {var subQ0=sQuery(id+"F2.wireOp",EDGE,"E16.9.0");Q26=makeQuery(id+"F2.imprint","IMPRINT",FACE,{"disambiguationData":[TD([[makeQuery(id+"F2.imprint","IMPRINT",EDGE,{"derivedFrom":subQ0}),1.0]])]});}
            var Q27;
            {var subQ0=sQuery(id+"F2.wireOp",EDGE,"E16.8.1");Q27=makeQuery(id+"F2.imprint","IMPRINT",FACE,{"disambiguationData":[TD([[makeQuery(id+"F2.imprint","IMPRINT",EDGE,{"derivedFrom":subQ0}),1.0]])]});}
            var Q28;
            {var subQ0=sQuery(id+"F2.wireOp",EDGE,"E16.8.0");Q28=makeQuery(id+"F2.imprint","IMPRINT",FACE,{"disambiguationData":[TD([[makeQuery(id+"F2.imprint","IMPRINT",EDGE,{"derivedFrom":subQ0}),1.0]])]});}
            var Q29;
            {var subQ0=sQuery(id+"F2.wireOp",EDGE,"E16.7.1");Q29=makeQuery(id+"F2.imprint","IMPRINT",FACE,{"disambiguationData":[TD([[makeQuery(id+"F2.imprint","IMPRINT",EDGE,{"derivedFrom":subQ0}),1.0]])]});}
            var Q30;
            {var subQ0=sQuery(id+"F2.wireOp",EDGE,"E16.7.0");Q30=makeQuery(id+"F2.imprint","IMPRINT",FACE,{"disambiguationData":[TD([[makeQuery(id+"F2.imprint","IMPRINT",EDGE,{"derivedFrom":subQ0}),1.0]])]});}
            var Q31;
            {var subQ0=sQuery(id+"F2.wireOp",EDGE,"E16.6.1");Q31=makeQuery(id+"F2.imprint","IMPRINT",FACE,{"disambiguationData":[TD([[makeQuery(id+"F2.imprint","IMPRINT",EDGE,{"derivedFrom":subQ0}),1.0]])]});}
            var Q32;
            {var subQ0=sQuery(id+"F2.wireOp",EDGE,"E16.6.0");Q32=makeQuery(id+"F2.imprint","IMPRINT",FACE,{"disambiguationData":[TD([[makeQuery(id+"F2.imprint","IMPRINT",EDGE,{"derivedFrom":subQ0}),1.0]])]});}
            var Q33;
            {var subQ0=sQuery(id+"F2.wireOp",EDGE,"E16.5.1");Q33=makeQuery(id+"F2.imprint","IMPRINT",FACE,{"disambiguationData":[TD([[makeQuery(id+"F2.imprint","IMPRINT",EDGE,{"derivedFrom":subQ0}),1.0]])]});}
            var Q34;
            {var subQ0=sQuery(id+"F2.wireOp",EDGE,"E16.5.0");Q34=makeQuery(id+"F2.imprint","IMPRINT",FACE,{"disambiguationData":[TD([[makeQuery(id+"F2.imprint","IMPRINT",EDGE,{"derivedFrom":subQ0}),1.0]])]});}
            var Q35;
            {var subQ0=sQuery(id+"F2.wireOp",EDGE,"E16.4.1");Q35=makeQuery(id+"F2.imprint","IMPRINT",FACE,{"disambiguationData":[TD([[makeQuery(id+"F2.imprint","IMPRINT",EDGE,{"derivedFrom":subQ0}),1.0]])]});}
            extrude(context, id + "F3", {"entities" : qUnion([Q0, Q1, Q2, Q3, Q4, Q5, Q6, Q7, Q8, Q9, Q10, Q11, Q12, Q13, Q14, Q15, Q16, Q17, Q18, Q19, Q20, Q21, Q22, Q23, Q24, Q25, Q26, Q27, Q28, Q29, Q30, Q31, Q32, Q33, Q34, Q35]), "operationType" : NewBodyOperationType.REMOVE, "oppositeDirection" : true, "depth" : 25.4 * mm});
        }
        {
            var Q0;
            Q0=makeQuery(id+"F1.opExtrude","SWEPT_EDGE",EDGE,{"disambiguationData":[OSD([sQuery(id+"F0.wireOp",EDGE,"E11"),sQuery(id+"F0.wireOp",EDGE,"E12.15.1")])]});
            var Q1;
            Q1=makeQuery(id+"F1.opExtrude","SWEPT_EDGE",EDGE,{"disambiguationData":[OSD([sQuery(id+"F0.wireOp",EDGE,"E11"),sQuery(id+"F0.wireOp",EDGE,"E12.16.1")])]});
            var Q2;
            Q2=makeQuery(id+"F1.opExtrude","SWEPT_EDGE",EDGE,{"disambiguationData":[OSD([sQuery(id+"F0.wireOp",EDGE,"E11"),sQuery(id+"F0.wireOp",EDGE,"E12.15.0")])]});
            var Q3;
            Q3=makeQuery(id+"F1.opExtrude","SWEPT_EDGE",EDGE,{"disambiguationData":[OSD([sQuery(id+"F0.wireOp",EDGE,"E11"),sQuery(id+"F0.wireOp",EDGE,"E12.17.1")])]});
            var Q4;
            Q4=makeQuery(id+"F1.opExtrude","SWEPT_EDGE",EDGE,{"disambiguationData":[OSD([sQuery(id+"F0.wireOp",EDGE,"E11"),sQuery(id+"F0.wireOp",EDGE,"E12.16.0")])]});
            var Q5;
            Q5=makeQuery(id+"F1.opExtrude","SWEPT_EDGE",EDGE,{"disambiguationData":[OSD([sQuery(id+"F0.wireOp",EDGE,"E11"),sQuery(id+"F0.wireOp",EDGE,"E12.17.0")])]});
            var Q6;
            Q6=makeQuery(id+"F1.opExtrude","SWEPT_EDGE",EDGE,{"disambiguationData":[OSD([sQuery(id+"F0.wireOp",EDGE,"E7"),sQuery(id+"F0.wireOp",EDGE,"E11")])]});
            var Q7;
            Q7=makeQuery(id+"F1.opExtrude","SWEPT_EDGE",EDGE,{"disambiguationData":[OSD([sQuery(id+"F0.wireOp",EDGE,"E6"),sQuery(id+"F0.wireOp",EDGE,"E11")])]});
            var Q8;
            Q8=makeQuery(id+"F1.opExtrude","SWEPT_EDGE",EDGE,{"disambiguationData":[OSD([sQuery(id+"F0.wireOp",EDGE,"E11"),sQuery(id+"F0.wireOp",EDGE,"E12.1.1")])]});
            var Q9;
            Q9=makeQuery(id+"F1.opExtrude","SWEPT_EDGE",EDGE,{"disambiguationData":[OSD([sQuery(id+"F0.wireOp",EDGE,"E11"),sQuery(id+"F0.wireOp",EDGE,"E12.1.0")])]});
            var Q10;
            Q10=makeQuery(id+"F1.opExtrude","SWEPT_EDGE",EDGE,{"disambiguationData":[OSD([sQuery(id+"F0.wireOp",EDGE,"E11"),sQuery(id+"F0.wireOp",EDGE,"E12.2.1")])]});
            var Q11;
            Q11=makeQuery(id+"F1.opExtrude","SWEPT_EDGE",EDGE,{"disambiguationData":[OSD([sQuery(id+"F0.wireOp",EDGE,"E11"),sQuery(id+"F0.wireOp",EDGE,"E12.2.0")])]});
            var Q12;
            Q12=makeQuery(id+"F1.opExtrude","SWEPT_EDGE",EDGE,{"disambiguationData":[OSD([sQuery(id+"F0.wireOp",EDGE,"E11"),sQuery(id+"F0.wireOp",EDGE,"E12.3.1")])]});
            var Q13;
            Q13=makeQuery(id+"F1.opExtrude","SWEPT_EDGE",EDGE,{"disambiguationData":[OSD([sQuery(id+"F0.wireOp",EDGE,"E11"),sQuery(id+"F0.wireOp",EDGE,"E12.3.0")])]});
            var Q14;
            Q14=makeQuery(id+"F1.opExtrude","SWEPT_EDGE",EDGE,{"disambiguationData":[OSD([sQuery(id+"F0.wireOp",EDGE,"E11"),sQuery(id+"F0.wireOp",EDGE,"E12.4.1")])]});
            var Q15;
            Q15=makeQuery(id+"F1.opExtrude","SWEPT_EDGE",EDGE,{"disambiguationData":[OSD([sQuery(id+"F0.wireOp",EDGE,"E11"),sQuery(id+"F0.wireOp",EDGE,"E12.4.0")])]});
            var Q16;
            Q16=makeQuery(id+"F1.opExtrude","SWEPT_EDGE",EDGE,{"disambiguationData":[OSD([sQuery(id+"F0.wireOp",EDGE,"E11"),sQuery(id+"F0.wireOp",EDGE,"E12.5.0")])]});
            var Q17;
            Q17=makeQuery(id+"F1.opExtrude","SWEPT_EDGE",EDGE,{"disambiguationData":[OSD([sQuery(id+"F0.wireOp",EDGE,"E11"),sQuery(id+"F0.wireOp",EDGE,"E12.5.1")])]});
            var Q18;
            Q18=makeQuery(id+"F1.opExtrude","SWEPT_EDGE",EDGE,{"disambiguationData":[OSD([sQuery(id+"F0.wireOp",EDGE,"E11"),sQuery(id+"F0.wireOp",EDGE,"E12.6.1")])]});
            var Q19;
            Q19=makeQuery(id+"F1.opExtrude","SWEPT_EDGE",EDGE,{"disambiguationData":[OSD([sQuery(id+"F0.wireOp",EDGE,"E11"),sQuery(id+"F0.wireOp",EDGE,"E12.6.0")])]});
            var Q20;
            Q20=makeQuery(id+"F1.opExtrude","SWEPT_EDGE",EDGE,{"disambiguationData":[OSD([sQuery(id+"F0.wireOp",EDGE,"E11"),sQuery(id+"F0.wireOp",EDGE,"E12.8.1")])]});
            var Q21;
            Q21=makeQuery(id+"F1.opExtrude","SWEPT_EDGE",EDGE,{"disambiguationData":[OSD([sQuery(id+"F0.wireOp",EDGE,"E11"),sQuery(id+"F0.wireOp",EDGE,"E12.8.0")])]});
            var Q22;
            Q22=makeQuery(id+"F1.opExtrude","SWEPT_EDGE",EDGE,{"disambiguationData":[OSD([sQuery(id+"F0.wireOp",EDGE,"E11"),sQuery(id+"F0.wireOp",EDGE,"E12.9.0")])]});
            var Q23;
            Q23=makeQuery(id+"F1.opExtrude","SWEPT_EDGE",EDGE,{"disambiguationData":[OSD([sQuery(id+"F0.wireOp",EDGE,"E11"),sQuery(id+"F0.wireOp",EDGE,"E12.9.1")])]});
            var Q24;
            Q24=makeQuery(id+"F1.opExtrude","SWEPT_EDGE",EDGE,{"disambiguationData":[OSD([sQuery(id+"F0.wireOp",EDGE,"E11"),sQuery(id+"F0.wireOp",EDGE,"E12.10.1")])]});
            var Q25;
            Q25=makeQuery(id+"F1.opExtrude","SWEPT_EDGE",EDGE,{"disambiguationData":[OSD([sQuery(id+"F0.wireOp",EDGE,"E11"),sQuery(id+"F0.wireOp",EDGE,"E12.11.1")])]});
            var Q26;
            Q26=makeQuery(id+"F1.opExtrude","SWEPT_EDGE",EDGE,{"disambiguationData":[OSD([sQuery(id+"F0.wireOp",EDGE,"E11"),sQuery(id+"F0.wireOp",EDGE,"E12.10.0")])]});
            var Q27;
            Q27=makeQuery(id+"F1.opExtrude","SWEPT_EDGE",EDGE,{"disambiguationData":[OSD([sQuery(id+"F0.wireOp",EDGE,"E11"),sQuery(id+"F0.wireOp",EDGE,"E12.11.0")])]});
            var Q28;
            Q28=makeQuery(id+"F1.opExtrude","SWEPT_EDGE",EDGE,{"disambiguationData":[OSD([sQuery(id+"F0.wireOp",EDGE,"E11"),sQuery(id+"F0.wireOp",EDGE,"E12.14.0")])]});
            var Q29;
            Q29=makeQuery(id+"F1.opExtrude","SWEPT_EDGE",EDGE,{"disambiguationData":[OSD([sQuery(id+"F0.wireOp",EDGE,"E11"),sQuery(id+"F0.wireOp",EDGE,"E12.14.1")])]});
            var Q30;
            Q30=makeQuery(id+"F1.opExtrude","SWEPT_EDGE",EDGE,{"disambiguationData":[OSD([sQuery(id+"F0.wireOp",EDGE,"E11"),sQuery(id+"F0.wireOp",EDGE,"E12.13.0")])]});
            var Q31;
            Q31=makeQuery(id+"F1.opExtrude","SWEPT_EDGE",EDGE,{"disambiguationData":[OSD([sQuery(id+"F0.wireOp",EDGE,"E11"),sQuery(id+"F0.wireOp",EDGE,"E12.13.1")])]});
            var Q32;
            Q32=makeQuery(id+"F1.opExtrude","SWEPT_EDGE",EDGE,{"disambiguationData":[OSD([sQuery(id+"F0.wireOp",EDGE,"E11"),sQuery(id+"F0.wireOp",EDGE,"E12.12.0")])]});
            var Q33;
            Q33=makeQuery(id+"F1.opExtrude","SWEPT_EDGE",EDGE,{"disambiguationData":[OSD([sQuery(id+"F0.wireOp",EDGE,"E11"),sQuery(id+"F0.wireOp",EDGE,"E12.12.1")])]});
            var Q34;
            Q34=makeQuery(id+"F1.opExtrude","SWEPT_EDGE",EDGE,{"disambiguationData":[OSD([sQuery(id+"F0.wireOp",EDGE,"E11"),sQuery(id+"F0.wireOp",EDGE,"E12.7.1")])]});
            var Q35;
            Q35=makeQuery(id+"F1.opExtrude","SWEPT_EDGE",EDGE,{"disambiguationData":[OSD([sQuery(id+"F0.wireOp",EDGE,"E11"),sQuery(id+"F0.wireOp",EDGE,"E12.7.0")])]});
            fillet(context, id + "F4", {"entities" : qUnion([Q0, Q1, Q2, Q3, Q4, Q5, Q6, Q7, Q8, Q9, Q10, Q11, Q12, Q13, Q14, Q15, Q16, Q17, Q18, Q19, Q20, Q21, Q22, Q23, Q24, Q25, Q26, Q27, Q28, Q29, Q30, Q31, Q32, Q33, Q34, Q35]), "radius" : 0.76 * mm, "tangentPropagation" : true, "allowEdgeOverflow" : false});
        }
    });
